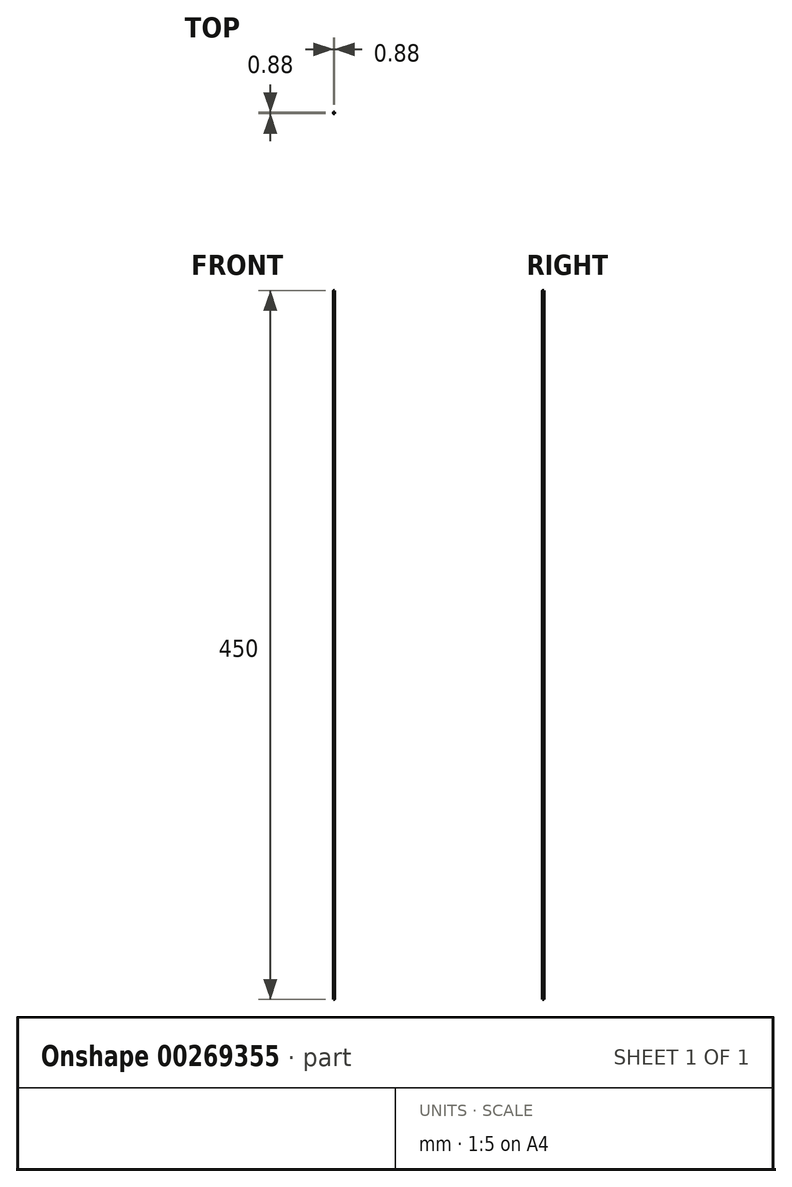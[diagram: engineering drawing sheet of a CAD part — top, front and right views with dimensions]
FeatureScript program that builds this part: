
annotation { "Feature Type Name" : "Feature", "Feature Type Description" : "" }
export const myFeature = defineFeature(function(context is Context, id is Id, definition is map)
    precondition{}
    {
        {
            var Q0;
            Q0=qCreatedBy(makeId("Top.planeOp"),FACE);
            var sketch = newSketch(context, id + "F0", { "sketchPlane" : qUnion([Q0])});
            skCircle(sketch, "E0", {"center": v(0, 0) * mm, "radius": 0.44 * mm});
            skSolve(sketch);
        }
        {
            var Q0;
            Q0 = qSketchRegion(id + "F0", true);
            extrude(context, id + "F1", {"entities" : qUnion([Q0]), "depth" : 450 * mm});
        }
    });
